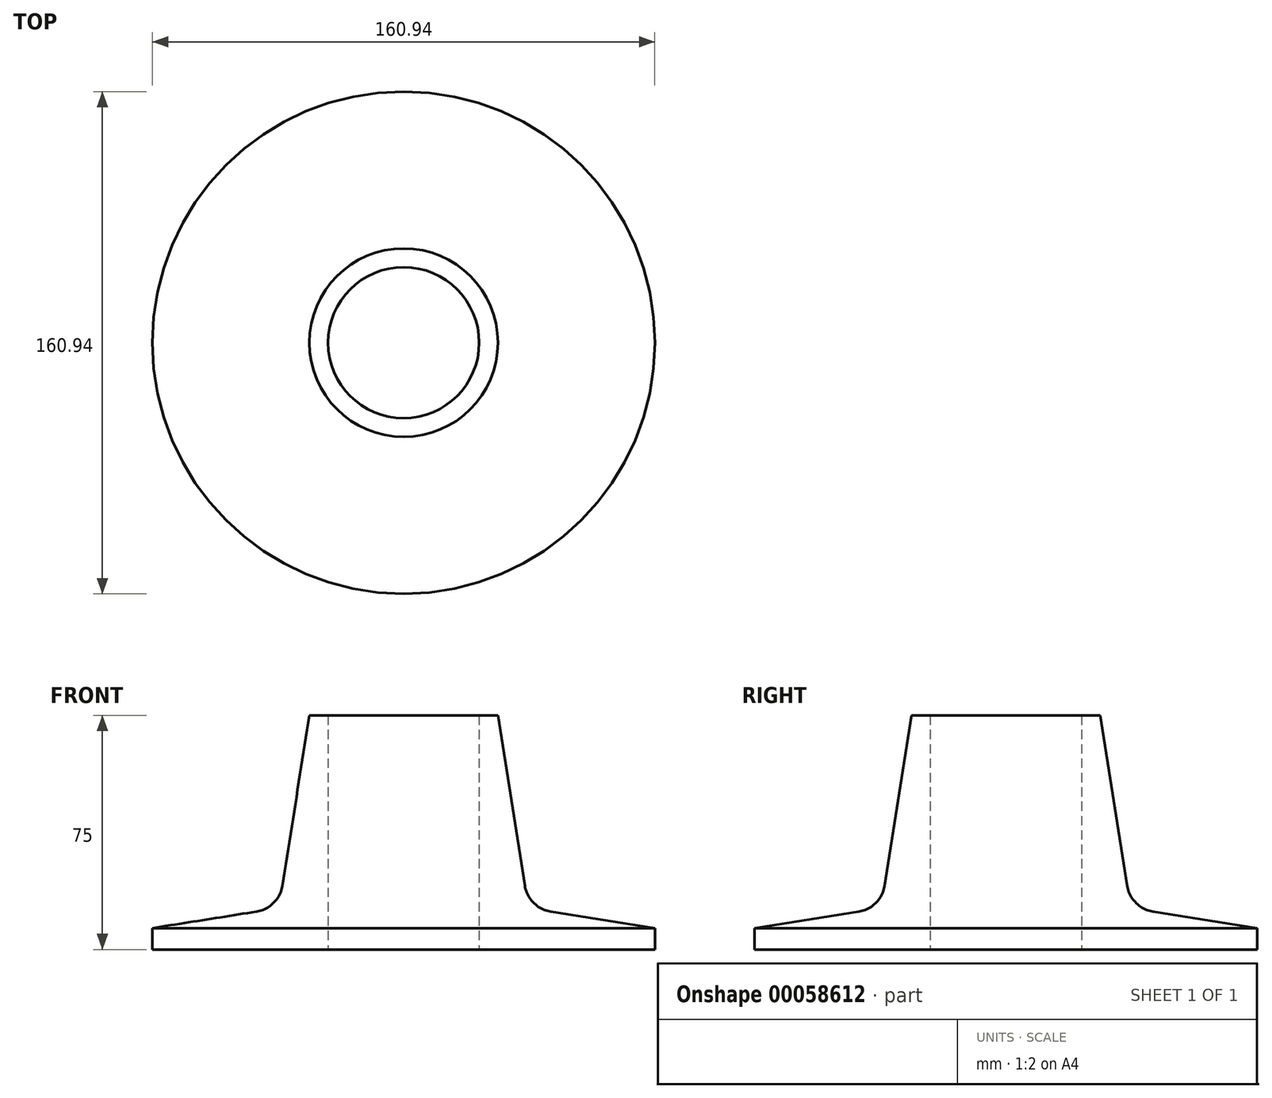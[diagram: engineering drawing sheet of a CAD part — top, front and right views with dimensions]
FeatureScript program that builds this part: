
annotation { "Feature Type Name" : "Feature", "Feature Type Description" : "" }
export const myFeature = defineFeature(function(context is Context, id is Id, definition is map)
    precondition{}
    {
        {
            var Q0;
            Q0=qCreatedBy(makeId("Front.planeOp"),FACE);
            var sketch = newSketch(context, id + "F0", { "sketchPlane" : qUnion([Q0])});
            skLineSegment(sketch, "E0", {"start": v(0, 0) * mm, "end": v(0, 75) * mm, "construction": true});
            skLineSegment(sketch, "E1", {"start": v(24.2, 0) * mm, "end": v(24.2, 75) * mm});
            skLineSegment(sketch, "E2", {"start": v(24.2, 75) * mm, "end": v(30.2, 75) * mm});
            skLineSegment(sketch, "E3", {"start": v(80.47, 6.86) * mm, "end": v(80.47, 0) * mm});
            skLineSegment(sketch, "E4", {"start": v(80.47, 0) * mm, "end": v(24.2, 0) * mm});
            skLineSegment(sketch, "E5", {"start": v(30.2, 75) * mm, "end": v(39.98, 13.27) * mm});
            skLineSegment(sketch, "E6", {"start": v(39.98, 13.27) * mm, "end": v(80.47, 6.86) * mm});
            skSolve(sketch);
        }
        {
            var Q0;
            Q0=makeQuery(id+"F0.imprint","IMPRINT",FACE,{"disambiguationData":[TD([[makeQuery(id+"F0.imprint","IMPRINT",EDGE,{"derivedFrom":sQuery(id+"F0.wireOp",EDGE,"E1")}),-1.0]])]});
            var Q1;
            Q1=sQuery(id+"F0.wireOp",EDGE,"E0");
            revolve(context, id + "F1", {"entities" : qUnion([Q0]), "axis" : qUnion([Q1]), "revolveType" : RevolveType.FULL});
        }
        {
            var Q0;
            Q0=makeQuery(id+"F1.opRevolve","SWEPT_EDGE",EDGE,{"disambiguationData":[OSD([sQuery(id+"F0.wireOp",EDGE,"E5"),sQuery(id+"F0.wireOp",EDGE,"E6")])]});
            fillet(context, id + "F2", {"entities" : qUnion([Q0]), "radius" : 10 * mm, "tangentPropagation" : true, "allowEdgeOverflow" : false});
        }
    });
